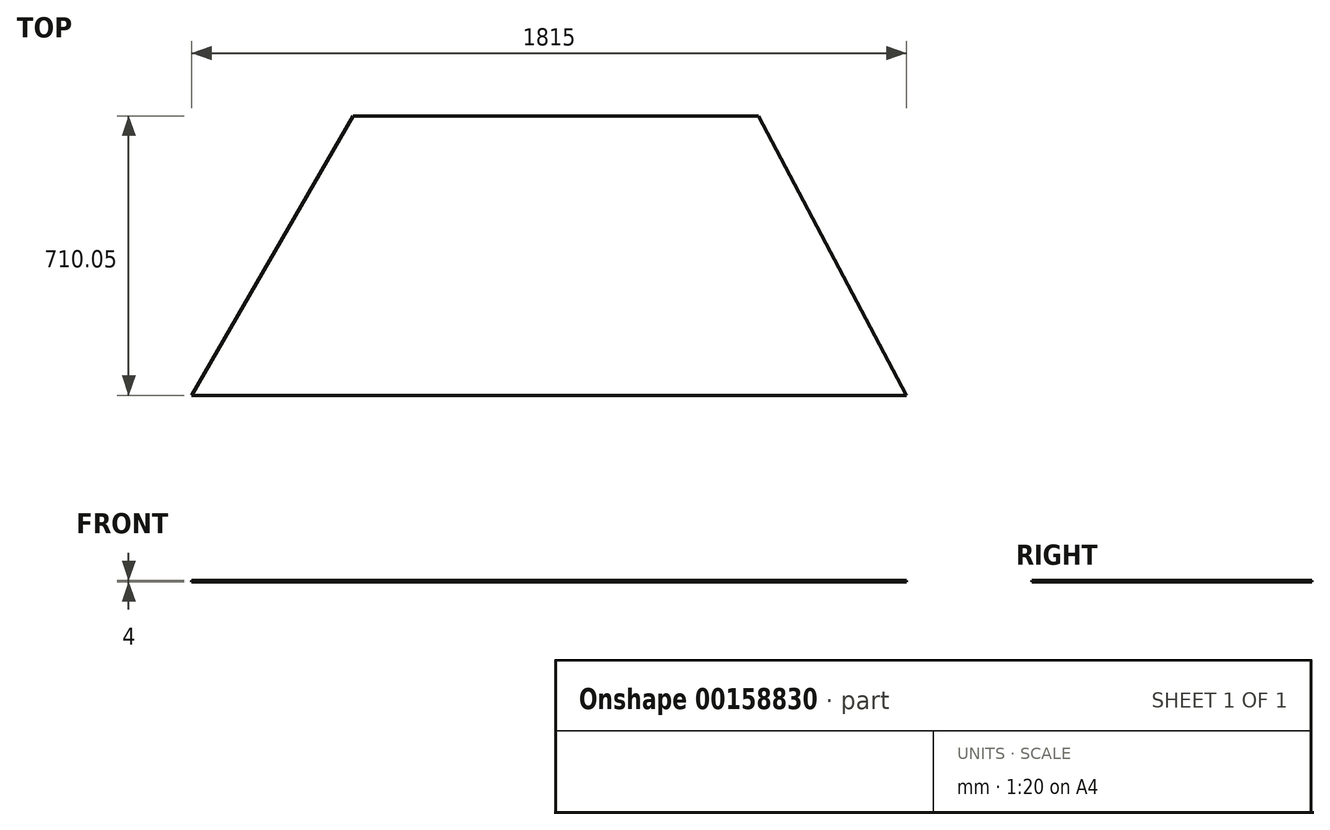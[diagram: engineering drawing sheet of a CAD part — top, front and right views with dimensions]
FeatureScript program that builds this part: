
annotation { "Feature Type Name" : "Feature", "Feature Type Description" : "" }
export const myFeature = defineFeature(function(context is Context, id is Id, definition is map)
    precondition{}
    {
        {
            var Q0;
            Q0=qCreatedBy(makeId("Top.planeOp"),FACE);
            var sketch = newSketch(context, id + "F0", { "sketchPlane" : qUnion([Q0])});
            skLineSegment(sketch, "E0", {"start": v(0, 0) * mm, "end": v(1815, 0) * mm});
            skLineSegment(sketch, "E1", {"start": v(1815, 0) * mm, "end": v(1439.95, 710.05) * mm});
            skLineSegment(sketch, "E2", {"start": v(1439.95, 710.05) * mm, "end": v(409.95, 710.05) * mm});
            skLineSegment(sketch, "E3", {"start": v(0, 0) * mm, "end": v(409.95, 710.05) * mm});
            skSolve(sketch);
        }
        {
            var Q0;
            Q0=qSketchRegion(id+"F0",true);
            extrude(context, id + "F1", {"entities" : qUnion([Q0]), "depth" : 4 * mm});
        }
    });
